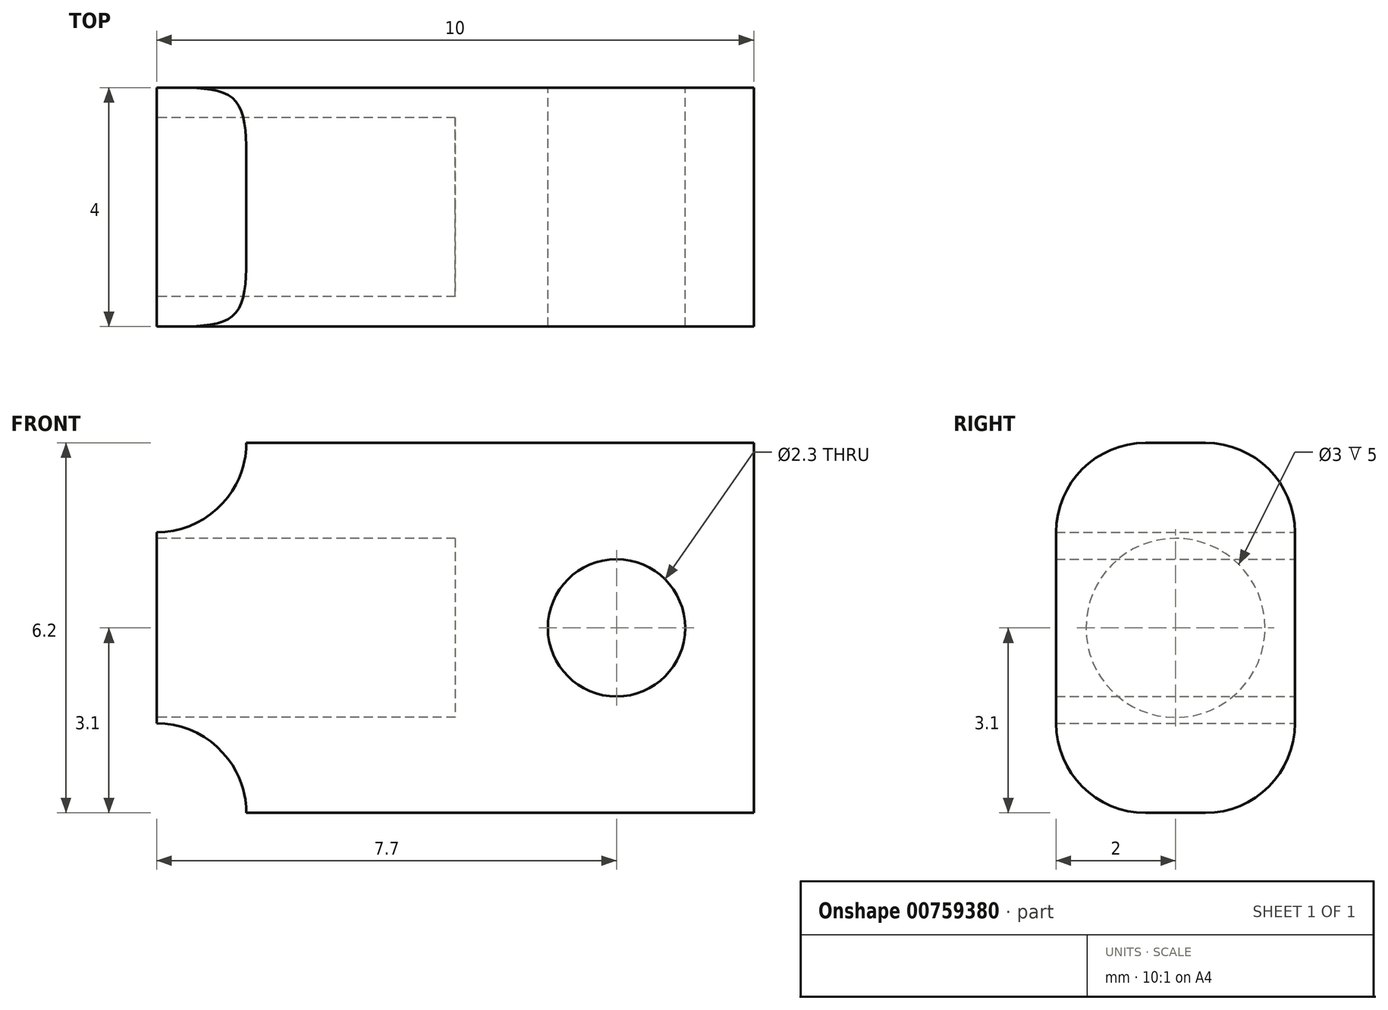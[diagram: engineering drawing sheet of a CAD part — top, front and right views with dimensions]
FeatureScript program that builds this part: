
annotation { "Feature Type Name" : "Feature", "Feature Type Description" : "" }
export const myFeature = defineFeature(function(context is Context, id is Id, definition is map)
    precondition{}
    {
        {
            var Q0;
            Q0=qCreatedBy(makeId("Front.planeOp"),FACE);
            var sketch = newSketch(context, id + "F0", { "sketchPlane" : qUnion([Q0])});
            skLineSegment(sketch, "E0.bottom", {"start": v(5, -3.1) * mm, "end": v(-3.5, -3.1) * mm});
            skLineSegment(sketch, "E0.top", {"start": v(5, 3.1) * mm, "end": v(-3.5, 3.1) * mm});
            skLineSegment(sketch, "E0.left", {"start": v(5, -3.1) * mm, "end": v(5, 3.1) * mm});
            skLineSegment(sketch, "E0.right", {"start": v(-5, -1.6) * mm, "end": v(-5, 1.6) * mm});
            skPoint(sketch, "E0.middle", {"position": v(0, 0) * mm});
            skArc(sketch, "E1", {"start": v(-5, 1.6) * mm, "mid": v(-3.94, 2.04) * mm, "end": v(-3.5, 3.1) * mm});
            skArc(sketch, "E2", {"start": v(-3.5, -3.1) * mm, "mid": v(-3.94, -2.04) * mm, "end": v(-5, -1.6) * mm});
            skCircle(sketch, "E3", {"center": v(2.7, 0) * mm, "radius": 1.15 * mm});
            skSolve(sketch);
        }
        {
            var Q0;
            Q0=makeQuery(id+"F0.imprint","IMPRINT",FACE,{"disambiguationData":[TD([[makeQuery(id+"F0.imprint","IMPRINT",EDGE,{"derivedFrom":sQuery(id+"F0.wireOp",EDGE,"E0.bottom")}),-1.0]])]});
            extrude(context, id + "F1", {"entities" : qUnion([Q0]), "depth" : 4 * mm, "offsetDistance" : 25 * mm});
        }
        {
            var Q0;
            Q0=makeQuery(id+"F1.opExtrude","SWEPT_FACE",FACE,{"disambiguationData":[OSD([sQuery(id+"F0.wireOp",EDGE,"E0.right")])]});
            var sketch = newSketch(context, id + "F2", { "sketchPlane" : qUnion([Q0])});
            skCircle(sketch, "E4", {"center": v(2, 0) * mm, "radius": 1.5 * mm});
            skPoint(sketch, "E4.centerSnap0", {"position": v(2, 1.6) * mm});
            skSolve(sketch);
        }
        {
            var Q0;
            Q0=makeQuery(id+"F2.imprint","IMPRINT",FACE,{"disambiguationData":[TD([[makeQuery(id+"F2.imprint","IMPRINT",EDGE,{"derivedFrom":sQuery(id+"F2.wireOp",EDGE,"E4")}),1.0]])]});
            extrude(context, id + "F3", {"entities" : qUnion([Q0]), "operationType" : NewBodyOperationType.REMOVE, "oppositeDirection" : true, "depth" : 5 * mm, "offsetDistance" : 25 * mm});
        }
        {
            var Q0;
            Q0=makeQuery(id+"F1.opExtrude","CAP_EDGE",EDGE,{"disambiguationData":[OSD([sQuery(id+"F0.wireOp",EDGE,"E0.bottom")])],"isStart":false});
            var Q1;
            Q1=makeQuery(id+"F1.opExtrude","CAP_EDGE",EDGE,{"disambiguationData":[OSD([sQuery(id+"F0.wireOp",EDGE,"E0.top")])],"isStart":false});
            var Q2;
            Q2=makeQuery(id+"F1.opExtrude","CAP_EDGE",EDGE,{"disambiguationData":[OSD([sQuery(id+"F0.wireOp",EDGE,"E0.bottom")])],"isStart":true});
            var Q3;
            Q3=makeQuery(id+"F1.opExtrude","CAP_EDGE",EDGE,{"disambiguationData":[OSD([sQuery(id+"F0.wireOp",EDGE,"E0.top")])],"isStart":true});
            fillet(context, id + "F4", {"entities" : qUnion([Q0, Q1, Q2, Q3]), "radius" : 1.5 * mm, "tangentPropagation" : true, "allowEdgeOverflow" : false});
        }
    });
